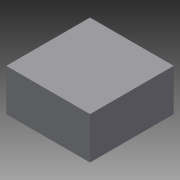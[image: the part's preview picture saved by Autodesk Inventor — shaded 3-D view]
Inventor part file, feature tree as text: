
AUTODESK INVENTOR PART (.ipt)
format: ipt  version: 2016 (Build 200138000, 138)  size: 68,608 bytes
history: native  units: in
note: dims shown in document units (in); Inventor stores cm internally (conversion verified against a paired STEP export)
features: extrude x1, sketch x1
ambient origin geometry x8: Origin, YZ Plane, XZ Plane, XY Plane, X Axis, Y Axis, Z Axis, Center Point
bodies: Solid1 (feature_tree)
feature tree (2):
  extrude  "Extrusion1"  Depth=2.2835in
  sketch  "Sketch1"  dims[d0=2.2835in d1=2.2835in d2=1.1417in d3=0.0in]
